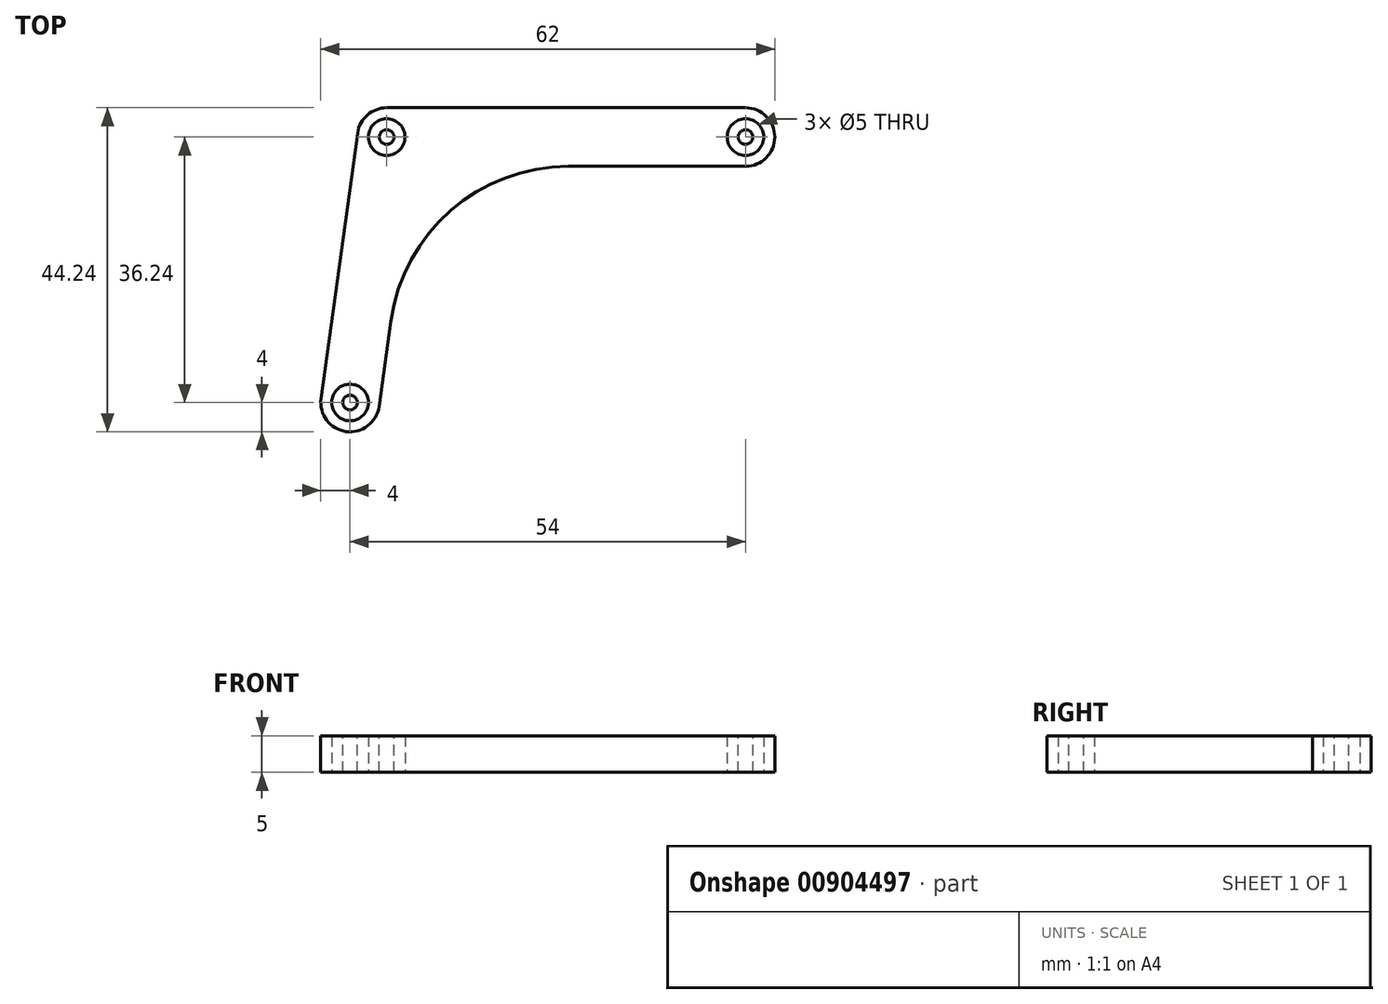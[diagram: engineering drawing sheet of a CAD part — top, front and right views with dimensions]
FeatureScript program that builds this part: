
annotation { "Feature Type Name" : "Feature", "Feature Type Description" : "" }
export const myFeature = defineFeature(function(context is Context, id is Id, definition is map)
    precondition{}
    {
        {
            var Q0;
            Q0=qCreatedBy(makeId("Top.planeOp"),FACE);
            var sketch = newSketch(context, id + "F0", { "sketchPlane" : qUnion([Q0])});
            skArc(sketch, "E0", {"start": v(0, 4) * mm, "mid": v(-2.63, 3.02) * mm, "end": v(-3.96, 0.55) * mm});
            skArc(sketch, "E1", {"start": v(49, -4) * mm, "mid": v(53, 0) * mm, "end": v(49, 4) * mm});
            skArc(sketch, "E2", {"start": v(-8.96, -35.7) * mm, "mid": v(-5.55, -40.2) * mm, "end": v(-1.04, -36.79) * mm});
            skCircle(sketch, "E3", {"center": v(0, 0) * mm, "radius": 2.5 * mm});
            skCircle(sketch, "E4", {"center": v(49, 0) * mm, "radius": 2.5 * mm});
            skCircle(sketch, "E5", {"center": v(-5, -36.24) * mm, "radius": 2.5 * mm});
            skLineSegment(sketch, "E6", {"start": v(-3.96, 0.55) * mm, "end": v(-8.96, -35.7) * mm});
            skLineSegment(sketch, "E7", {"start": v(-1.04, -36.79) * mm, "end": v(0.57, -25.15) * mm});
            skLineSegment(sketch, "E8", {"start": v(49, -4) * mm, "end": v(24.84, -4) * mm});
            skLineSegment(sketch, "E9", {"start": v(0, 4) * mm, "end": v(49, 4) * mm});
            skArc(sketch, "E10", {"start": v(24.84, -4) * mm, "mid": v(8.74, -10.03) * mm, "end": v(0.57, -25.15) * mm});
            skCircle(sketch, "E11", {"center": v(0, 0) * mm, "radius": 1 * mm});
            skCircle(sketch, "E12", {"center": v(49, 0) * mm, "radius": 1 * mm});
            skCircle(sketch, "E13", {"center": v(-5, -36.24) * mm, "radius": 1 * mm});
            skSolve(sketch);
        }
        {
            var Q0;
            Q0=makeQuery(id+"F0.imprint","IMPRINT",FACE,{"disambiguationData":[TD([[makeQuery(id+"F0.imprint","IMPRINT",EDGE,{"derivedFrom":sQuery(id+"F0.wireOp",EDGE,"E0")}),1.0]])]});
            extrude(context, id + "F1", {"entities" : qUnion([Q0]), "endBound" : BoundingType.SYMMETRIC, "depth" : 5 * mm, "offsetDistance" : 25.4 * mm});
        }
        {
            var Q0;
            Q0=makeQuery(id+"F1.opExtrude","CAP_FACE",FACE,{"disambiguationData":[OSD([sQuery(id+"F0.wireOp",EDGE,"E0"),sQuery(id+"F0.wireOp",EDGE,"E1"),sQuery(id+"F0.wireOp",EDGE,"E2"),sQuery(id+"F0.wireOp",EDGE,"E3"),sQuery(id+"F0.wireOp",EDGE,"E4"),sQuery(id+"F0.wireOp",EDGE,"E5"),sQuery(id+"F0.wireOp",EDGE,"E6"),sQuery(id+"F0.wireOp",EDGE,"E7"),sQuery(id+"F0.wireOp",EDGE,"E8"),sQuery(id+"F0.wireOp",EDGE,"E9"),sQuery(id+"F0.wireOp",EDGE,"E10")])],"isStart":false});
            var sketch = newSketch(context, id + "F2", { "sketchPlane" : qUnion([Q0])});
            skCircle(sketch, "E14", {"center": v(0, 0) * mm, "radius": 1 * mm});
            skCircle(sketch, "E15", {"center": v(49, 0) * mm, "radius": 1 * mm});
            skCircle(sketch, "E16", {"center": v(-5, -36.24) * mm, "radius": 1 * mm});
            skSolve(sketch);
        }
        {
            var Q0;
            Q0=makeQuery(id+"F2.imprint","IMPRINT",FACE,{"disambiguationData":[TD([[makeQuery(id+"F2.imprint","IMPRINT",EDGE,{"derivedFrom":sQuery(id+"F2.wireOp",EDGE,"E14")}),1.0]])]});
            var Q1;
            Q1=makeQuery(id+"F2.imprint","IMPRINT",FACE,{"disambiguationData":[TD([[makeQuery(id+"F2.imprint","IMPRINT",EDGE,{"derivedFrom":sQuery(id+"F2.wireOp",EDGE,"E16")}),1.0]])]});
            var Q2;
            Q2=makeQuery(id+"F2.imprint","IMPRINT",FACE,{"disambiguationData":[TD([[makeQuery(id+"F2.imprint","IMPRINT",EDGE,{"derivedFrom":sQuery(id+"F2.wireOp",EDGE,"E15")}),1.0]])]});
            extrude(context, id + "F3", {"entities" : qUnion([Q0, Q1, Q2]), "oppositeDirection" : true, "depth" : 5 * mm, "offsetDistance" : 25.4 * mm});
        }
    });
